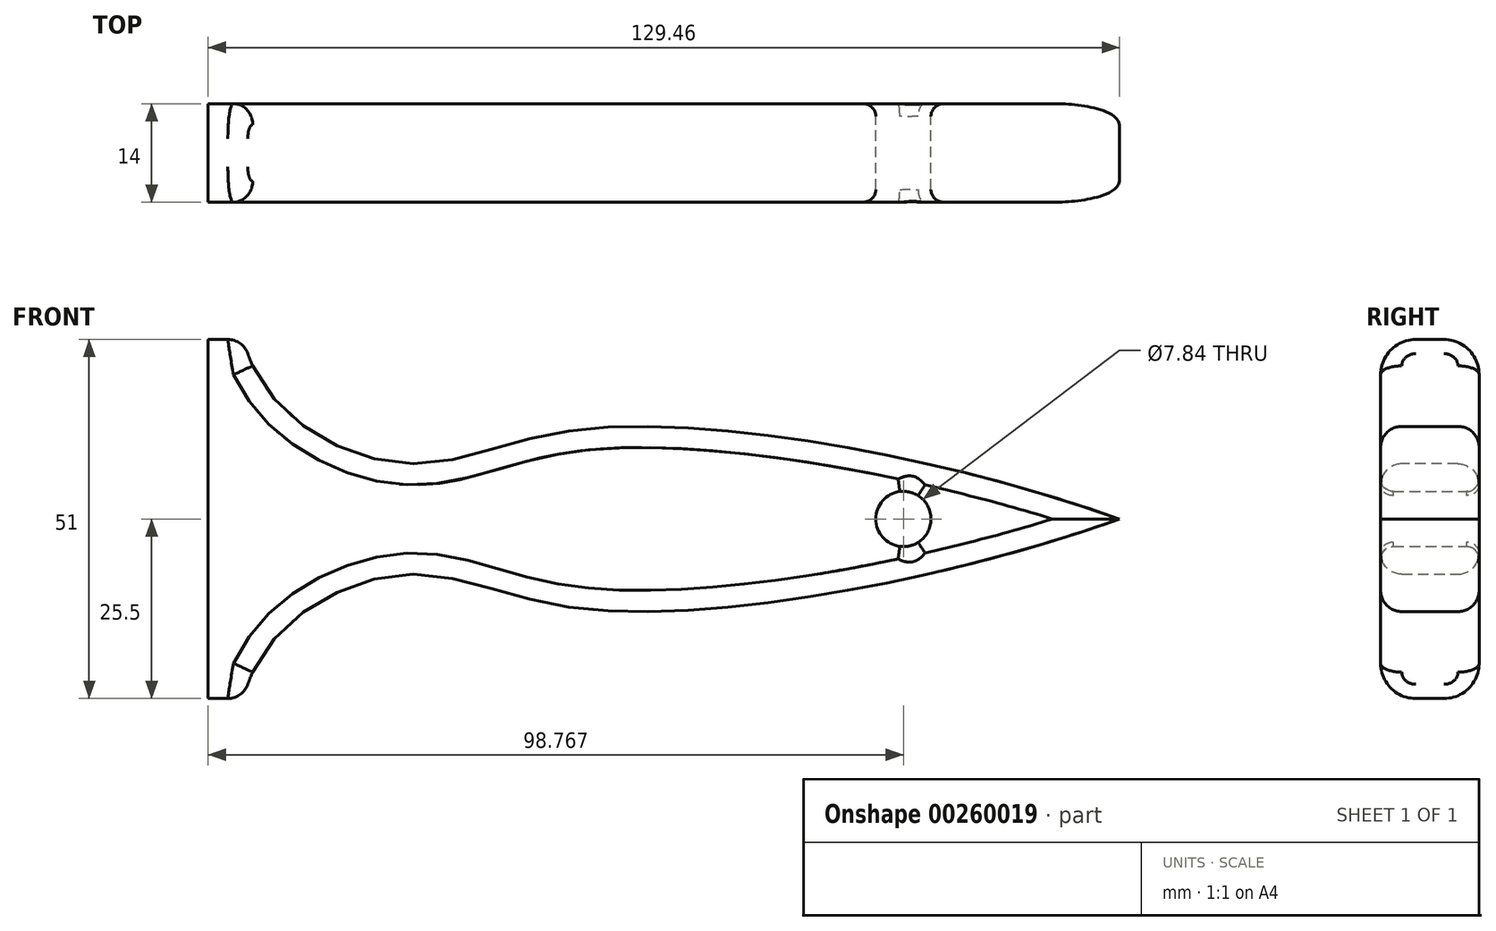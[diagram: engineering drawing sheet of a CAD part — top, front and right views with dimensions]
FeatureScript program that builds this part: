
annotation { "Feature Type Name" : "Feature", "Feature Type Description" : "" }
export const myFeature = defineFeature(function(context is Context, id is Id, definition is map)
    precondition{}
    {
        {
            var Q0;
            Q0=qCreatedBy(makeId("Front.planeOp"),FACE);
            var sketch = newSketch(context, id + "F0", { "sketchPlane" : qUnion([Q0])});
            skLineSegment(sketch, "E0.right", {"start": v(-64.73, -25.5) * mm, "end": v(-64.73, 25.5) * mm});
            skPoint(sketch, "E0.middle", {"position": v(0, 0) * mm});
            skFitSpline(sketch, "E1", {"points": [v(-59.66, 25.5) * mm, v(-37.25, 7.92) * mm, v(-12.41, 12.65) * mm, v(64.73, 0) * mm], "startDerivative": vector(26.12, -116.2) * mm, "endDerivative": vector(160.12, -57.33) * mm});
            skFitSpline(sketch, "E2.MirrorCS", {"points": [v(-59.66, -25.5) * mm, v(-37.25, -7.92) * mm, v(-12.41, -12.65) * mm, v(64.73, 0) * mm], "startDerivative": vector(26.12, 116.2) * mm, "endDerivative": vector(160.12, 57.33) * mm});
            skLineSegment(sketch, "E3", {"start": v(-59.66, 25.5) * mm, "end": v(-64.73, 25.5) * mm});
            skLineSegment(sketch, "E4", {"start": v(-64.73, -25.5) * mm, "end": v(-59.66, -25.5) * mm});
            skSolve(sketch);
        }
        {
            var Q0;
            Q0=makeQuery(id+"F0.imprint","IMPRINT",FACE,{"disambiguationData":[TD([[makeQuery(id+"F0.imprint","IMPRINT",EDGE,{"derivedFrom":sQuery(id+"F0.wireOp",EDGE,"E0.right")}),-1.0]])]});
            extrude(context, id + "F1", {"entities" : qUnion([Q0]), "endBound" : BoundingType.SYMMETRIC, "depth" : 14 * mm});
        }
        {
            var Q0;
            Q0=makeQuery(id+"F1.opExtrude","CAP_EDGE",EDGE,{"disambiguationData":[OSD([sQuery(id+"F0.wireOp",EDGE,"E4")])],"isStart":false});
            var Q1;
            Q1=makeQuery(id+"F1.opExtrude","CAP_EDGE",EDGE,{"disambiguationData":[OSD([sQuery(id+"F0.wireOp",EDGE,"E4")])],"isStart":true});
            var Q2;
            Q2=makeQuery(id+"F1.opExtrude","CAP_EDGE",EDGE,{"disambiguationData":[OSD([sQuery(id+"F0.wireOp",EDGE,"E3")])],"isStart":false});
            var Q3;
            Q3=makeQuery(id+"F1.opExtrude","CAP_EDGE",EDGE,{"disambiguationData":[OSD([sQuery(id+"F0.wireOp",EDGE,"E3")])],"isStart":true});
            fillet(context, id + "F2", {"entities" : qUnion([Q0, Q1, Q2, Q3]), "radius" : 5 * mm, "tangentPropagation" : true, "allowEdgeOverflow" : false});
        }
        {
            var Q0;
            Q0=makeQuery(id+"F1.opExtrude","CAP_EDGE",EDGE,{"disambiguationData":[OSD([sQuery(id+"F0.wireOp",EDGE,"E1")])],"isStart":false});
            var Q1;
            Q1=makeQuery(id+"F1.opExtrude","CAP_EDGE",EDGE,{"disambiguationData":[OSD([sQuery(id+"F0.wireOp",EDGE,"E2.MirrorCS")])],"isStart":false});
            fillet(context, id + "F3", {"entities" : qUnion([Q0, Q1]), "radius" : 3 * mm, "tangentPropagation" : true, "allowEdgeOverflow" : false});
        }
        {
            var Q0;
            Q0=qCreatedBy(makeId("Front.planeOp"),FACE);
            var sketch = newSketch(context, id + "F4", { "sketchPlane" : qUnion([Q0])});
            skCircle(sketch, "E5", {"center": v(34.04, 0) * mm, "radius": 3.92 * mm});
            skSolve(sketch);
        }
        {
            var Q0;
            Q0=qSketchRegion(id+"F4",true);
            extrude(context, id + "F5", {"entities" : qUnion([Q0]), "operationType" : NewBodyOperationType.REMOVE, "endBound" : BoundingType.SYMMETRIC, "depth" : 25 * mm});
        }
        {
            var Q0;
            Q0=makeQuery(id+"F5.boolean.opBoolean","INTERSECT",EDGE,{"derivedFrom":[makeQuery(id+"F1.opExtrude","CAP_FACE",FACE,{"disambiguationData":[OSD([sQuery(id+"F0.wireOp",EDGE,"E0.right"),sQuery(id+"F0.wireOp",EDGE,"E1"),sQuery(id+"F0.wireOp",EDGE,"E2.MirrorCS"),sQuery(id+"F0.wireOp",EDGE,"E3"),sQuery(id+"F0.wireOp",EDGE,"E4")])],"isStart":true}),makeQuery(id+"F5.opExtrude","SWEPT_FACE",FACE,{"disambiguationData":[OSD([sQuery(id+"F4.wireOp",EDGE,"E5")])]})]});
            var Q1;
            Q1=makeQuery(id+"F5.boolean.opBoolean","INTERSECT",EDGE,{"derivedFrom":[makeQuery(id+"F1.opExtrude","CAP_FACE",FACE,{"disambiguationData":[OSD([sQuery(id+"F0.wireOp",EDGE,"E0.right"),sQuery(id+"F0.wireOp",EDGE,"E1"),sQuery(id+"F0.wireOp",EDGE,"E2.MirrorCS"),sQuery(id+"F0.wireOp",EDGE,"E3"),sQuery(id+"F0.wireOp",EDGE,"E4")])],"isStart":false}),makeQuery(id+"F5.opExtrude","SWEPT_FACE",FACE,{"disambiguationData":[OSD([sQuery(id+"F4.wireOp",EDGE,"E5")])]})]});
            fillet(context, id + "F6", {"entities" : qUnion([Q0, Q1]), "radius" : 1.8 * mm, "tangentPropagation" : true, "allowEdgeOverflow" : false});
        }
    });
